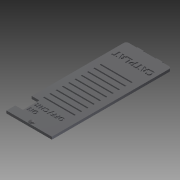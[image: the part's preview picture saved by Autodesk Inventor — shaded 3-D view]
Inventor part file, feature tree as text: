
AUTODESK INVENTOR PART (.ipt)
format: ipt  version: 2015 (Build 190159000, 159)  size: 417,280 bytes
history: native  units: mm
features: sketch x6, extrude x5, other x1, chamfer x1, hole x1
ambient origin geometry x8: Origin, YZ Plane, XZ Plane, XY Plane, X Axis, Y Axis, Z Axis, Center Point
bodies: Body1 (feature_tree)
feature tree (14):
  other  "Sólido1"
  extrude  "Extrusión1"  Depth=95.0mm
  extrude  "Extrusión2"  Depth=2.0mm TaperAngle=0.0deg
  chamfer  "Chaflán1"  Distance=1.5mm
  extrude  "Extrusión3"  Depth=0.8mm
  hole  "Agujero1"  [1 undecoded]
  extrude  "Extrusión4"  Depth=5.0mm
  extrude  "Extrusión5"  Depth=0.8mm TaperAngle=0.0deg
  sketch  "Boceto1"  dims[d0=36.0mm d1=95.0mm]
  sketch  "Boceto2"  dims[d2=2.0mm d5=2.0mm d6=0.0mm]
  sketch  "Boceto3"  dims[d7=5.0mm]
  sketch  "Boceto4"  dims[d8=1.0mm]
  sketch  "Boceto5"  dims[d9=10.0mm d10=1.5mm d11=0.0mm]
  sketch  "Boceto6"  dims[d12=0.5mm d13=2.0mm d14=45.0deg d15=25.0mm d16=1.0mm d17=100.0mm d19=5.0mm d20=10.0mm d22=10.0mm d24=2.0mm d25=0.0mm d26=2.5mm d27=2.4mm d28=6.0mm d29=4.6mm d30=2.0mm d31=90.0deg d32=8.0mm d33=20.594885mm d35=0.5mm d37=6.0mm d38=13.0mm d39=20.0mm d40=10.0mm d41=0.0mm d42=0.8mm d43=0.0mm]
note: 1 required parameter value undecoded (feature->parameter linkage not recoverable at this tier; creation-order binding heuristic only, values carry confidence <= 0.55)
